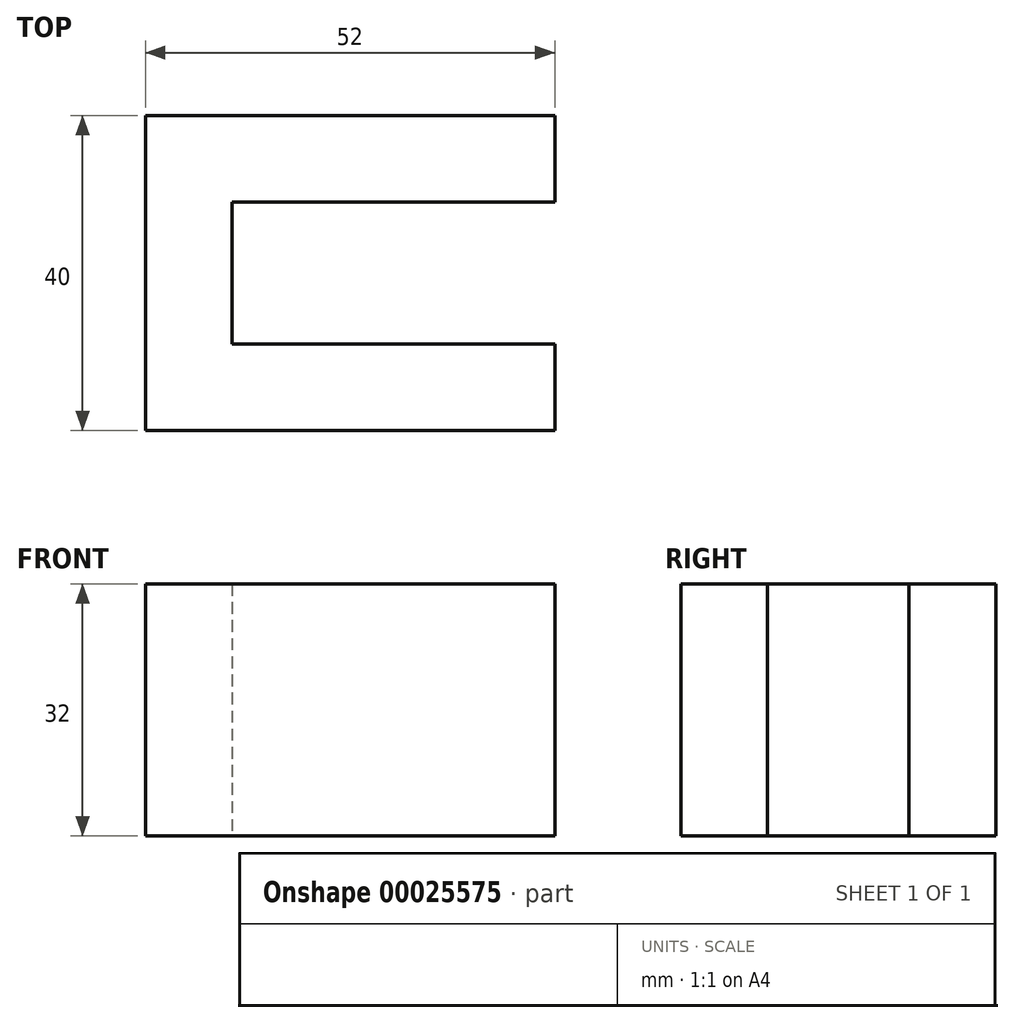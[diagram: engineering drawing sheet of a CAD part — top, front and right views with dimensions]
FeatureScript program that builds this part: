
annotation { "Feature Type Name" : "Feature", "Feature Type Description" : "" }
export const myFeature = defineFeature(function(context is Context, id is Id, definition is map)
    precondition{}
    {
        {
            var Q0;
            Q0=qCreatedBy(makeId("Right.planeOp"),FACE);
            var sketch = newSketch(context, id + "F0", { "sketchPlane" : qUnion([Q0])});
            skLineSegment(sketch, "E0.bottom", {"start": v(-24.61, 13.7) * mm, "end": v(15.39, 13.7) * mm});
            skLineSegment(sketch, "E0.top", {"start": v(-24.61, -18.3) * mm, "end": v(15.39, -18.3) * mm});
            skLineSegment(sketch, "E0.left", {"start": v(-24.61, 13.7) * mm, "end": v(-24.61, -18.3) * mm});
            skLineSegment(sketch, "E0.right", {"start": v(15.39, 13.7) * mm, "end": v(15.39, -18.3) * mm});
            skLineSegment(sketch, "E1", {"start": v(-13.61, 13.7) * mm, "end": v(-13.61, -18.3) * mm});
            skLineSegment(sketch, "E2", {"start": v(4.39, 13.7) * mm, "end": v(4.39, -18.3) * mm});
            skSolve(sketch);
        }
        {
            var Q0;
            {var subQ1=sQuery(id+"F0.wireOp",EDGE,"E0.left");Q0=makeQuery(id+"F0.imprint","IMPRINT",FACE,{"disambiguationData":[TD([[makeQuery(id+"F0.imprint","IMPRINT",EDGE,{"derivedFrom":subQ1}),1.0]])]});}
            var Q1;
            {var subQ1=sQuery(id+"F0.wireOp",EDGE,"E1");Q1=makeQuery(id+"F0.imprint","IMPRINT",FACE,{"disambiguationData":[TD([[makeQuery(id+"F0.imprint","IMPRINT",EDGE,{"derivedFrom":subQ1}),1.0]])]});}
            var Q2;
            {var subQ1=sQuery(id+"F0.wireOp",EDGE,"E0.right");Q2=makeQuery(id+"F0.imprint","IMPRINT",FACE,{"disambiguationData":[TD([[makeQuery(id+"F0.imprint","IMPRINT",EDGE,{"derivedFrom":subQ1}),-1.0]])]});}
            extrude(context, id + "F1", {"entities" : qUnion([Q0, Q1, Q2]), "depth" : 11 * mm});
        }
        {
            var Q0;
            Q0=makeQuery(id+"F1.opExtrude","CAP_FACE",FACE,{"disambiguationData":[OSD([sQuery(id+"F0.wireOp",EDGE,"E0.bottom"),sQuery(id+"F0.wireOp",EDGE,"E0.top"),sQuery(id+"F0.wireOp",EDGE,"E0.left"),sQuery(id+"F0.wireOp",EDGE,"E0.right")])],"isStart":false});
            var sketch = newSketch(context, id + "F2", { "sketchPlane" : qUnion([Q0])});
            skLineSegment(sketch, "E3", {"start": v(-13.61, 13.7) * mm, "end": v(-13.61, -18.3) * mm});
            skLineSegment(sketch, "E4", {"start": v(4.39, 13.7) * mm, "end": v(4.39, -18.3) * mm});
            skSolve(sketch);
        }
        {
            var Q0;
            {var subQ1=sQuery(id+"F2.wireOp",EDGE,"E3");Q0=makeQuery(id+"F2.imprint","IMPRINT",FACE,{"disambiguationData":[TD([[makeQuery(id+"F2.imprint","IMPRINT",EDGE,{"derivedFrom":subQ1}),-1.0]])]});}
            var Q1;
            {var subQ1=sQuery(id+"F2.wireOp",EDGE,"E4");Q1=makeQuery(id+"F2.imprint","IMPRINT",FACE,{"disambiguationData":[TD([[makeQuery(id+"F2.imprint","IMPRINT",EDGE,{"derivedFrom":subQ1}),1.0]])]});}
            extrude(context, id + "F3", {"entities" : qUnion([Q0, Q1]), "operationType" : NewBodyOperationType.ADD, "depth" : 41 * mm});
        }
    });
